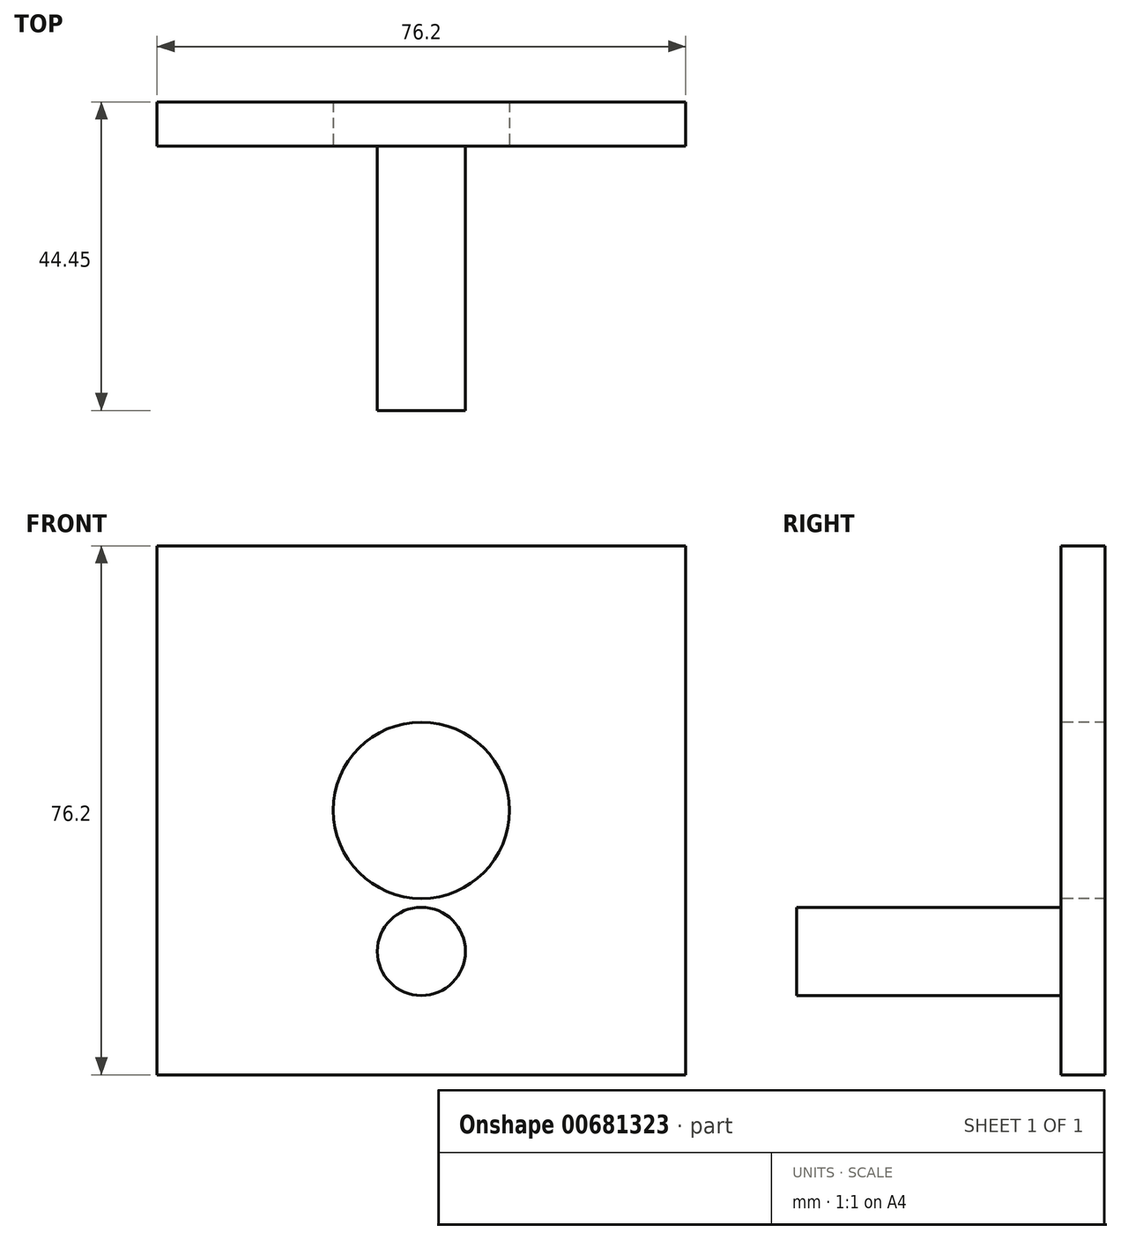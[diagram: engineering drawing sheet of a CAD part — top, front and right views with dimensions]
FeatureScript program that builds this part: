
annotation { "Feature Type Name" : "Feature", "Feature Type Description" : "" }
export const myFeature = defineFeature(function(context is Context, id is Id, definition is map)
    precondition{}
    {
        {
            var Q0;
            Q0=qCreatedBy(makeId("Front.planeOp"),FACE);
            var sketch = newSketch(context, id + "F0", { "sketchPlane" : qUnion([Q0])});
            skLineSegment(sketch, "E0", {"start": v(0, 0) * mm, "end": v(0, 76.2) * mm});
            skLineSegment(sketch, "E1", {"start": v(0, 76.2) * mm, "end": v(76.2, 76.2) * mm});
            skLineSegment(sketch, "E2", {"start": v(76.2, 76.2) * mm, "end": v(76.2, 0) * mm});
            skLineSegment(sketch, "E3", {"start": v(76.2, 0) * mm, "end": v(0, 0) * mm});
            skSolve(sketch);
        }
        {
            var Q0;
            Q0=makeQuery(id+"F0.imprint","IMPRINT",FACE,{"disambiguationData":[TD([[makeQuery(id+"F0.imprint","IMPRINT",EDGE,{"derivedFrom":sQuery(id+"F0.wireOp",EDGE,"E0")}),-1.0]])]});
            extrude(context, id + "F1", {"entities" : qUnion([Q0]), "depth" : 6.35 * mm, "offsetDistance" : 25.4 * mm});
        }
        {
            var Q0;
            Q0=makeQuery(id+"F1.opExtrude","CAP_FACE",FACE,{"disambiguationData":[OSD([sQuery(id+"F0.wireOp",EDGE,"E0"),sQuery(id+"F0.wireOp",EDGE,"E1"),sQuery(id+"F0.wireOp",EDGE,"E2"),sQuery(id+"F0.wireOp",EDGE,"E3")])],"isStart":false});
            var sketch = newSketch(context, id + "F2", { "sketchPlane" : qUnion([Q0])});
            skCircle(sketch, "E4", {"center": v(38.1, 38.1) * mm, "radius": 12.7 * mm});
            skSolve(sketch);
        }
        {
            var Q0;
            Q0=makeQuery(id+"F2.imprint","IMPRINT",FACE,{"disambiguationData":[TD([[makeQuery(id+"F2.imprint","IMPRINT",EDGE,{"derivedFrom":sQuery(id+"F2.wireOp",EDGE,"E4")}),1.0]])]});
            extrude(context, id + "F3", {"entities" : qUnion([Q0]), "operationType" : NewBodyOperationType.REMOVE, "oppositeDirection" : true, "depth" : 25.4 * mm, "offsetDistance" : 25.4 * mm});
        }
        {
            var Q0;
            Q0=makeQuery(id+"F1.opExtrude","CAP_FACE",FACE,{"disambiguationData":[OSD([sQuery(id+"F0.wireOp",EDGE,"E0"),sQuery(id+"F0.wireOp",EDGE,"E1"),sQuery(id+"F0.wireOp",EDGE,"E2"),sQuery(id+"F0.wireOp",EDGE,"E3")])],"isStart":false});
            var sketch = newSketch(context, id + "F4", { "sketchPlane" : qUnion([Q0])});
            skCircle(sketch, "E5", {"center": v(38.1, 17.78) * mm, "radius": 6.35 * mm});
            skSolve(sketch);
        }
        {
            var Q0;
            Q0=makeQuery(id+"F4.imprint","IMPRINT",FACE,{"disambiguationData":[TD([[makeQuery(id+"F4.imprint","IMPRINT",EDGE,{"derivedFrom":sQuery(id+"F4.wireOp",EDGE,"E5")}),1.0]])]});
            extrude(context, id + "F5", {"entities" : qUnion([Q0]), "operationType" : NewBodyOperationType.ADD, "depth" : 38.1 * mm, "offsetDistance" : 25.4 * mm});
        }
    });
